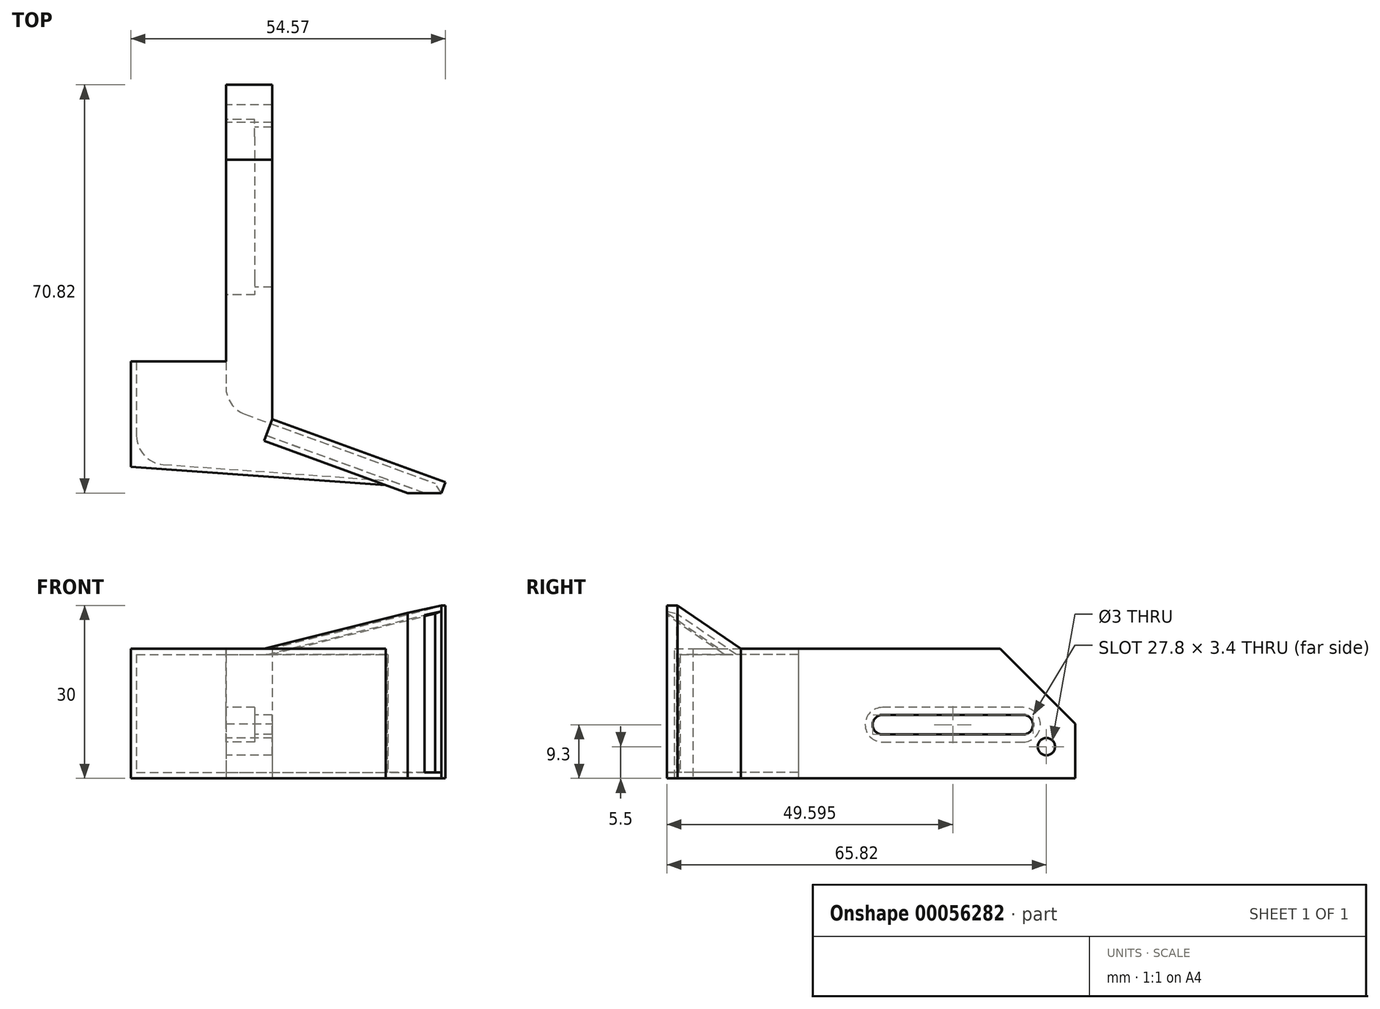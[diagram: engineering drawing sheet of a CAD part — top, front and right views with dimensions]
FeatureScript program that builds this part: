
annotation { "Feature Type Name" : "Feature", "Feature Type Description" : "" }
export const myFeature = defineFeature(function(context is Context, id is Id, definition is map)
    precondition{}
    {
        {
            var Q0;
            Q0=qCreatedBy(makeId("Top.planeOp"),FACE);
            var sketch = newSketch(context, id + "F0", { "sketchPlane" : qUnion([Q0])});
            skLineSegment(sketch, "E0", {"start": v(0, 0) * mm, "end": v(0, 18.27) * mm});
            skLineSegment(sketch, "E1", {"start": v(0, 18.27) * mm, "end": v(24.5, 18.27) * mm});
            skLineSegment(sketch, "E2", {"start": v(24.5, 18.27) * mm, "end": v(24.5, 8.27) * mm});
            skLineSegment(sketch, "E3", {"start": v(24.5, 8.27) * mm, "end": v(48.9, -0.61) * mm});
            skLineSegment(sketch, "E4", {"start": v(48.9, -0.61) * mm, "end": v(47.88, -3.43) * mm});
            skLineSegment(sketch, "E5", {"start": v(47.88, -3.43) * mm, "end": v(0, 0) * mm});
            skSolve(sketch);
        }
        {
            var Q0;
            Q0=qSketchRegion(id+"F0",true);
            extrude(context, id + "F1", {"entities" : qUnion([Q0]), "depth" : 1 * mm});
        }
        {
            var Q0;
            Q0=makeQuery(id+"F1.opExtrude","CAP_FACE",FACE,{"disambiguationData":[OSD([sQuery(id+"F0.wireOp",EDGE,"E0"),sQuery(id+"F0.wireOp",EDGE,"E1"),sQuery(id+"F0.wireOp",EDGE,"E2"),sQuery(id+"F0.wireOp",EDGE,"E3"),sQuery(id+"F0.wireOp",EDGE,"E4"),sQuery(id+"F0.wireOp",EDGE,"E5")])],"isStart":false});
            var sketch = newSketch(context, id + "F2", { "sketchPlane" : qUnion([Q0])});
            skLineSegment(sketch, "E6", {"start": v(0, 18.27) * mm, "end": v(1, 18.27) * mm});
            skLineSegment(sketch, "E7", {"start": v(1, 18.27) * mm, "end": v(1, 0.73) * mm});
            skLineSegment(sketch, "E8", {"start": v(1, 0.73) * mm, "end": v(48.16, -2.65) * mm});
            skLineSegment(sketch, "E9", {"start": v(48.16, -2.65) * mm, "end": v(47.88, -3.43) * mm});
            skLineSegment(sketch, "E10", {"start": v(24.5, 18.27) * mm, "end": v(16.5, 18.27) * mm});
            skLineSegment(sketch, "E11", {"start": v(16.5, 18.27) * mm, "end": v(16.5, 10.33) * mm});
            skLineSegment(sketch, "E12", {"start": v(16.5, 10.33) * mm, "end": v(48.63, -1.36) * mm});
            skSolve(sketch);
        }
        {
            var Q0;
            Q0=qSketchRegion(id+"F2",true);
            var Q1;
            Q1=makeQuery(id+"F2.imprint","IMPRINT",FACE,{"disambiguationData":[TD([[makeQuery(id+"F2.imprint","IMPRINT",EDGE,{"derivedFrom":sQuery(id+"F2.wireOp",EDGE,"E6")}),-1.0]])]});
            var Q2;
            Q2=makeQuery(id+"F2.imprint","IMPRINT",FACE,{"disambiguationData":[TD([[makeQuery(id+"F2.imprint","IMPRINT",EDGE,{"derivedFrom":sQuery(id+"F2.wireOp",EDGE,"E10")}),-1.0]])]});
            extrude(context, id + "F3", {"entities" : qUnion([Q0, Q1, Q2]), "operationType" : NewBodyOperationType.ADD, "depth" : 20.5 * mm});
        }
        {
            var Q0;
            Q0=makeQuery(id+"F3.opExtrude","CAP_FACE",FACE,{"disambiguationData":[OSD([sQuery(id+"F0.wireOp",EDGE,"E2"),sQuery(id+"F0.wireOp",EDGE,"E3"),sQuery(id+"F0.wireOp",EDGE,"E4"),sQuery(id+"F2.wireOp",EDGE,"E10"),sQuery(id+"F2.wireOp",EDGE,"E11"),sQuery(id+"F2.wireOp",EDGE,"E12")])],"isStart":false});
            var sketch = newSketch(context, id + "F4", { "sketchPlane" : qUnion([Q0])});
            skLineSegment(sketch, "E13", {"start": v(0, 0) * mm, "end": v(0, 18.27) * mm});
            skLineSegment(sketch, "E14", {"start": v(0, 18.27) * mm, "end": v(24.5, 18.27) * mm});
            skLineSegment(sketch, "E15", {"start": v(24.5, 18.27) * mm, "end": v(24.5, 8.27) * mm});
            skLineSegment(sketch, "E16", {"start": v(24.5, 8.27) * mm, "end": v(48.9, -0.61) * mm});
            skLineSegment(sketch, "E17", {"start": v(48.9, -0.61) * mm, "end": v(47.88, -3.43) * mm});
            skLineSegment(sketch, "E18", {"start": v(47.88, -3.43) * mm, "end": v(0, 0) * mm});
            skSolve(sketch);
        }
        {
            var Q0;
            Q0=qSketchRegion(id+"F4",true);
            extrude(context, id + "F5", {"entities" : qUnion([Q0]), "operationType" : NewBodyOperationType.ADD, "depth" : 1 * mm});
        }
        {
            var Q0;
            Q0=makeQuery(id+"F1.opExtrude","CAP_FACE",FACE,{"disambiguationData":[OSD([sQuery(id+"F0.wireOp",EDGE,"E0"),sQuery(id+"F0.wireOp",EDGE,"E1"),sQuery(id+"F0.wireOp",EDGE,"E2"),sQuery(id+"F0.wireOp",EDGE,"E3"),sQuery(id+"F0.wireOp",EDGE,"E4"),sQuery(id+"F0.wireOp",EDGE,"E5")])],"isStart":true});
            var sketch = newSketch(context, id + "F6", { "sketchPlane" : qUnion([Q0])});
            skLineSegment(sketch, "E19", {"start": v(16.5, -66.27) * mm, "end": v(16.5, -18.27) * mm});
            skLineSegment(sketch, "E20.bottom", {"start": v(16.5, -18.27) * mm, "end": v(24.5, -18.27) * mm});
            skLineSegment(sketch, "E20.top", {"start": v(16.5, -66.27) * mm, "end": v(24.5, -66.27) * mm});
            skLineSegment(sketch, "E20.right", {"start": v(24.5, -18.27) * mm, "end": v(24.5, -66.27) * mm});
            skSolve(sketch);
        }
        {
            var Q0;
            Q0=qSketchRegion(id+"F6",true);
            var Q1;
            {var subQ2=sQuery(id+"F6.wireOp",EDGE,"edd6656e-1237-41b9-a912-baa1d064ff13");Q1=makeQuery(id+"F6.imprint","IMPRINT",FACE,{"disambiguationData":[TD([[makeQuery(id+"F6.imprint","IMPRINT",EDGE,{"derivedFrom":subQ2}),-1.0]])]});}
            var Q2;
            Q2=makeQuery(id+"F5.opExtrude","CAP_FACE",FACE,{"disambiguationData":[OSD([sQuery(id+"F4.wireOp",EDGE,"E13"),sQuery(id+"F4.wireOp",EDGE,"E14"),sQuery(id+"F4.wireOp",EDGE,"E15"),sQuery(id+"F4.wireOp",EDGE,"E16"),sQuery(id+"F4.wireOp",EDGE,"E17"),sQuery(id+"F4.wireOp",EDGE,"E18")])],"isStart":false});
            extrude(context, id + "F7", {"entities" : qUnion([Q0, Q1]), "operationType" : NewBodyOperationType.ADD, "endBound" : BoundingType.UP_TO_SURFACE, "oppositeDirection" : true, "endBoundEntityFace" : qUnion([Q2]), "depth" : 22 * mm});
        }
        {
            var Q0;
            Q0=makeQuery(id+"F7.boolean.opBoolean","MERGE",FACE,{"derivedFrom":[makeQuery(id+"F3.opExtrude","SWEPT_FACE",FACE,{"disambiguationData":[OSD([sQuery(id+"F2.wireOp",EDGE,"E11")])]}),makeQuery(id+"F7.opExtrude","SWEPT_FACE",FACE,{"disambiguationData":[OSD([sQuery(id+"F6.wireOp",EDGE,"E19")])]})]});
            var sketch = newSketch(context, id + "F8", { "sketchPlane" : qUnion([Q0])});
            skCircle(sketch, "E21", {"center": v(-61.27, 5.5) * mm, "radius": 1.5 * mm});
            skPoint(sketch, "E21.centerSnap0", {"position": v(-66.27, 11.25) * mm});
            skArc(sketch, "E22", {"start": v(-57.25, 11) * mm, "mid": v(-58.95, 9.3) * mm, "end": v(-57.25, 7.6) * mm});
            skArc(sketch, "E23", {"start": v(-32.85, 7.6) * mm, "mid": v(-31.15, 9.3) * mm, "end": v(-32.85, 11) * mm});
            skLineSegment(sketch, "E24", {"start": v(-57.25, 11) * mm, "end": v(-32.85, 11) * mm});
            skLineSegment(sketch, "E25", {"start": v(-57.25, 7.6) * mm, "end": v(-32.85, 7.6) * mm});
            skArc(sketch, "E26", {"start": v(-57.25, 12.3) * mm, "mid": v(-60.25, 9.3) * mm, "end": v(-57.25, 6.3) * mm});
            skArc(sketch, "E27", {"start": v(-32.85, 6.3) * mm, "mid": v(-29.85, 9.3) * mm, "end": v(-32.85, 12.3) * mm});
            skLineSegment(sketch, "E28", {"start": v(-57.25, 12.3) * mm, "end": v(-32.85, 12.3) * mm});
            skLineSegment(sketch, "E29", {"start": v(-32.85, 6.3) * mm, "end": v(-57.25, 6.3) * mm});
            skSolve(sketch);
        }
        {
            var Q0;
            Q0=makeQuery(id+"F8.imprint","IMPRINT",FACE,{"disambiguationData":[TD([[makeQuery(id+"F8.imprint","IMPRINT",EDGE,{"derivedFrom":sQuery(id+"F8.wireOp",EDGE,"E21")}),1.0]])]});
            var Q1;
            Q1=makeQuery(id+"F8.imprint","IMPRINT",FACE,{"disambiguationData":[TD([[makeQuery(id+"F8.imprint","IMPRINT",EDGE,{"derivedFrom":sQuery(id+"F8.wireOp",EDGE,"E22")}),1.0]])]});
            extrude(context, id + "F9", {"entities" : qUnion([Q0, Q1]), "operationType" : NewBodyOperationType.REMOVE, "oppositeDirection" : true, "depth" : 25 * mm});
        }
        {
            var Q0;
            Q0=makeQuery(id+"F8.imprint","IMPRINT",FACE,{"disambiguationData":[TD([[makeQuery(id+"F8.imprint","IMPRINT",EDGE,{"derivedFrom":sQuery(id+"F8.wireOp",EDGE,"E22")}),-1.0]])]});
            extrude(context, id + "F10", {"entities" : qUnion([Q0]), "operationType" : NewBodyOperationType.REMOVE, "oppositeDirection" : true, "depth" : 5 * mm});
        }
        {
            var Q0;
            Q0=makeQuery(id+"F3.opExtrude","SWEPT_EDGE",EDGE,{"disambiguationData":[OSD([sQuery(id+"F2.wireOp",EDGE,"E7"),sQuery(id+"F2.wireOp",EDGE,"E8")])]});
            var Q1;
            Q1=makeQuery(id+"F3.opExtrude","SWEPT_EDGE",EDGE,{"disambiguationData":[OSD([sQuery(id+"F2.wireOp",EDGE,"E11"),sQuery(id+"F2.wireOp",EDGE,"E12")])]});
            fillet(context, id + "F11", {"entities" : qUnion([Q0, Q1]), "radius" : 5 * mm, "tangentPropagation" : true, "allowEdgeOverflow" : false});
        }
        {
            var Q0;
            Q0=makeQuery(id+"F7.opExtrude","CAP_EDGE",EDGE,{"disambiguationData":[OSD([sQuery(id+"F6.wireOp",EDGE,"E20.top")])],"isStart":false});
            chamfer(context, id + "F12", {"entities" : qUnion([Q0]), "width" : 13 * mm, "tangentPropagation" : true});
        }
        {
            var Q0;
            {var subQ0=sQuery(id+"F0.wireOp",EDGE,"E3");Q0=makeQuery(id+"F5.boolean.opBoolean","MERGE",FACE,{"derivedFrom":[makeQuery(id+"F3.boolean.opBoolean","MERGE",FACE,{"derivedFrom":[makeQuery(id+"F1.opExtrude","SWEPT_FACE",FACE,{"disambiguationData":[OSD([subQ0])]}),makeQuery(id+"F3.opExtrude","SWEPT_FACE",FACE,{"disambiguationData":[OSD([subQ0])]})]}),makeQuery(id+"F5.opExtrude","SWEPT_FACE",FACE,{"disambiguationData":[OSD([sQuery(id+"F4.wireOp",EDGE,"E16")])]})]});}
            var sketch = newSketch(context, id + "F13", { "sketchPlane" : qUnion([Q0])});
            skLineSegment(sketch, "E30", {"start": v(-52.2, 30) * mm, "end": v(-20.2, 22.5) * mm});
            skLineSegment(sketch, "E31", {"start": v(-20.2, 0) * mm, "end": v(-52.2, 0) * mm});
            skLineSegment(sketch, "E32", {"start": v(-52.2, 0) * mm, "end": v(-52.2, 30) * mm});
            skLineSegment(sketch, "E33", {"start": v(-20.2, 22.5) * mm, "end": v(-20.2, 0) * mm});
            skSolve(sketch);
        }
        {
            var Q0;
            Q0 = qSketchRegion(id + "F13", true);
            var Q1;
            Q1=makeQuery(id+"F13.imprint","IMPRINT",FACE,{"disambiguationData":[TD([[makeQuery(id+"F13.imprint","IMPRINT",EDGE,{"derivedFrom":sQuery(id+"F13.wireOp",EDGE,"E30")}),-1.0]])]});
            extrude(context, id + "F14", {"entities" : qUnion([Q0, Q1]), "operationType" : NewBodyOperationType.ADD, "oppositeDirection" : true, "depth" : 3 * mm});
        }
        {
            var Q0;
            {var subQ0=sQuery(id+"F0.wireOp",EDGE,"E3");Q0=makeQuery(id+"F14.boolean.opBoolean","MERGE",FACE,{"derivedFrom":[makeQuery(id+"F5.boolean.opBoolean","MERGE",FACE,{"derivedFrom":[makeQuery(id+"F3.boolean.opBoolean","MERGE",FACE,{"derivedFrom":[makeQuery(id+"F1.opExtrude","SWEPT_FACE",FACE,{"disambiguationData":[OSD([subQ0])]}),makeQuery(id+"F3.opExtrude","SWEPT_FACE",FACE,{"disambiguationData":[OSD([subQ0])]})]}),makeQuery(id+"F5.opExtrude","SWEPT_FACE",FACE,{"disambiguationData":[OSD([sQuery(id+"F4.wireOp",EDGE,"E16")])]})]}),makeQuery(id+"F14.opExtrude","CAP_FACE",FACE,{"disambiguationData":[OSD([sQuery(id+"F13.wireOp",EDGE,"E30"),sQuery(id+"F13.wireOp",EDGE,"E31"),sQuery(id+"F13.wireOp",EDGE,"E32"),sQuery(id+"F13.wireOp",EDGE,"E33")])],"isStart":true})]});}
            var sketch = newSketch(context, id + "F15", { "sketchPlane" : qUnion([Q0])});
            skLineSegment(sketch, "E34", {"start": v(-20.2, 21.47) * mm, "end": v(-20.2, 1) * mm});
            skLineSegment(sketch, "E35", {"start": v(-20.2, 1) * mm, "end": v(-52.2, 1) * mm});
            skLineSegment(sketch, "E36", {"start": v(-52.2, 1) * mm, "end": v(-52.2, 28.97) * mm});
            skLineSegment(sketch, "E37", {"start": v(-52.2, 28.97) * mm, "end": v(-20.2, 21.47) * mm});
            skSolve(sketch);
        }
        {
            var Q0;
            Q0 = qSketchRegion(id + "F15", true);
            var Q1;
            {var subQ1=sQuery(id+"F0.wireOp",EDGE,"E5");var subQ2=sQuery(id+"F13.wireOp",EDGE,"E31");var subQ7=sQuery(id+"F13.wireOp",EDGE,"E30");var subQ8=sQuery(id+"F13.wireOp",EDGE,"E32");Q1=makeQuery(id+"F14.boolean.opBoolean","SPLIT",FACE,{"disambiguationData":[TD([makeQuery(id+"F1.opExtrude","SWEPT_FACE",FACE,{"disambiguationData":[OSD([subQ1])]})])],"derivedFrom":makeQuery(id+"F14.opExtrude","CAP_FACE",FACE,{"disambiguationData":[OSD([subQ7,subQ2,subQ8,sQuery(id+"F13.wireOp",EDGE,"E33")])],"isStart":false})});}
            extrude(context, id + "F16", {"entities" : qUnion([Q0]), "operationType" : NewBodyOperationType.REMOVE, "endBound" : BoundingType.UP_TO_SURFACE, "oppositeDirection" : true, "endBoundEntityFace" : qUnion([Q1]), "depth" : 25 * mm});
        }
        {
            var Q0;
            Q0=makeQuery(id+"F16.boolean.opBoolean","COPY",FACE,{"derivedFrom":makeQuery(id+"F16.opExtrude","SWEPT_FACE",FACE,{"disambiguationData":[OSD([sQuery(id+"F15.wireOp",EDGE,"E34")])]})});
            var Q1;
            {var subQ7=sQuery(id+"F13.wireOp",EDGE,"E32");var subQ8=sQuery(id+"F13.wireOp",EDGE,"E31");Q1=makeQuery(id+"F16.boolean.opBoolean","SPLIT",FACE,{"disambiguationData":[TD([makeQuery(id+"F14.opExtrude","SWEPT_FACE",FACE,{"disambiguationData":[OSD([subQ8])]})])],"derivedFrom":makeQuery(id+"F14.opExtrude","SWEPT_FACE",FACE,{"disambiguationData":[OSD([subQ7])]})});}
            extrude(context, id + "F17", {"entities" : qUnion([Q0]), "operationType" : NewBodyOperationType.ADD, "endBound" : BoundingType.UP_TO_SURFACE, "endBoundEntityFace" : qUnion([Q1]), "depth" : 25 * mm});
        }
        {
            var Q0;
            Q0=makeQuery(id+"F17.opExtrude","SWEPT_FACE",FACE,{"disambiguationData":[OSD([sQuery(id+"F0.wireOp",EDGE,"E2"),sQuery(id+"F0.wireOp",EDGE,"E3"),sQuery(id+"F4.wireOp",EDGE,"E15"),sQuery(id+"F4.wireOp",EDGE,"E16"),sQuery(id+"F15.wireOp",EDGE,"E34"),sQuery(id+"F15.wireOp",EDGE,"E37")])]});
            var Q1;
            Q1=makeQuery(id+"F16.boolean.opBoolean","COPY",FACE,{"derivedFrom":makeQuery(id+"F16.opExtrude","SWEPT_FACE",FACE,{"disambiguationData":[OSD([sQuery(id+"F15.wireOp",EDGE,"E37")])]})});
            extrude(context, id + "F18", {"entities" : qUnion([Q0]), "operationType" : NewBodyOperationType.ADD, "endBound" : BoundingType.UP_TO_SURFACE, "endBoundEntityFace" : qUnion([Q1]), "depth" : 25 * mm});
        }
        {
            var Q0;
            {var subQ0=sQuery(id+"F13.wireOp",EDGE,"E30");var subQ1=makeQuery(id+"F14.opExtrude","SWEPT_FACE",FACE,{"disambiguationData":[OSD([subQ0])]});var subQ7=sQuery(id+"F13.wireOp",EDGE,"E32");var subQ12=sQuery(id+"F0.wireOp",EDGE,"E5");var subQ13=sQuery(id+"F13.wireOp",EDGE,"E31");Q0=makeQuery(id+"F16.boolean.opBoolean","SPLIT",FACE,{"disambiguationData":[TD([subQ1])],"derivedFrom":makeQuery(id+"F14.boolean.opBoolean","SPLIT",FACE,{"disambiguationData":[TD([makeQuery(id+"F1.opExtrude","SWEPT_FACE",FACE,{"disambiguationData":[OSD([subQ12])]})])],"derivedFrom":makeQuery(id+"F14.opExtrude","CAP_FACE",FACE,{"disambiguationData":[OSD([subQ0,subQ13,subQ7,sQuery(id+"F13.wireOp",EDGE,"E33")])],"isStart":false})})});}
            var Q1;
            {var subQ0=sQuery(id+"F0.wireOp",EDGE,"E5");var subQ2=sQuery(id+"F13.wireOp",EDGE,"E31");var subQ4=makeQuery(id+"F1.opExtrude","SWEPT_FACE",FACE,{"disambiguationData":[OSD([subQ0])]});var subQ18=sQuery(id+"F13.wireOp",EDGE,"E32");var subQ21=sQuery(id+"F13.wireOp",EDGE,"E30");Q1=makeQuery(id+"F16.boolean.opBoolean","SPLIT",FACE,{"disambiguationData":[TD([subQ4])],"derivedFrom":makeQuery(id+"F14.boolean.opBoolean","SPLIT",FACE,{"disambiguationData":[TD([subQ4])],"derivedFrom":makeQuery(id+"F14.opExtrude","CAP_FACE",FACE,{"disambiguationData":[OSD([subQ21,subQ2,subQ18,sQuery(id+"F13.wireOp",EDGE,"E33")])],"isStart":false})})});}
            extrude(context, id + "F19", {"entities" : qUnion([Q0, Q1]), "operationType" : NewBodyOperationType.ADD, "depth" : 1 * mm});
        }
        {
            var Q0;
            Q0=makeQuery(id+"F19.opExtrude","SWEPT_FACE",FACE,{"disambiguationData":[OSD([sQuery(id+"F0.wireOp",EDGE,"E4"),sQuery(id+"F0.wireOp",EDGE,"E5"),sQuery(id+"F2.wireOp",EDGE,"E9"),sQuery(id+"F4.wireOp",EDGE,"E17"),sQuery(id+"F4.wireOp",EDGE,"E18")])]});
            var Q1;
            {var subQ0=sQuery(id+"F0.wireOp",EDGE,"E5");Q1=makeQuery(id+"F5.boolean.opBoolean","MERGE",FACE,{"derivedFrom":[makeQuery(id+"F3.boolean.opBoolean","MERGE",FACE,{"derivedFrom":[makeQuery(id+"F1.opExtrude","SWEPT_FACE",FACE,{"disambiguationData":[OSD([subQ0])]}),makeQuery(id+"F3.opExtrude","SWEPT_FACE",FACE,{"disambiguationData":[OSD([subQ0])]})]}),makeQuery(id+"F5.opExtrude","SWEPT_FACE",FACE,{"disambiguationData":[OSD([sQuery(id+"F4.wireOp",EDGE,"E18")])]})]});}
            extrude(context, id + "F20", {"entities" : qUnion([Q0]), "operationType" : NewBodyOperationType.ADD, "endBound" : BoundingType.UP_TO_SURFACE, "endBoundEntityFace" : qUnion([Q1]), "depth" : 25 * mm});
        }
        {
            var Q0;
            {var subQ0=sQuery(id+"F4.wireOp",EDGE,"E18");var subQ1=sQuery(id+"F4.wireOp",EDGE,"E17");var subQ2=sQuery(id+"F0.wireOp",EDGE,"E5");var subQ3=sQuery(id+"F0.wireOp",EDGE,"E4");var subQ5=sQuery(id+"F13.wireOp",EDGE,"E31");var subQ7=makeQuery(id+"F1.opExtrude","SWEPT_FACE",FACE,{"disambiguationData":[OSD([subQ2])]});var subQ19=sQuery(id+"F13.wireOp",EDGE,"E32");var subQ22=sQuery(id+"F13.wireOp",EDGE,"E30");var subQ23=sQuery(id+"F13.wireOp",EDGE,"E33");Q0=makeQuery(id+"F20.boolean.opBoolean","MERGE",FACE,{"derivedFrom":[makeQuery(id+"F19.opExtrude","CAP_FACE",FACE,{"disambiguationData":[OSD([subQ22,subQ5,subQ19,subQ23]),TDD([makeQuery(id+"F16.boolean.opBoolean","SPLIT",FACE,{"disambiguationData":[TD([subQ7])],"derivedFrom":makeQuery(id+"F14.boolean.opBoolean","SPLIT",FACE,{"disambiguationData":[TD([subQ7])],"derivedFrom":makeQuery(id+"F14.opExtrude","CAP_FACE",FACE,{"disambiguationData":[OSD([subQ22,subQ5,subQ19,subQ23])],"isStart":false})})})])],"isStart":false}),makeQuery(id+"F20.opExtrude","SWEPT_FACE",FACE,{"disambiguationData":[OSD([subQ3,subQ2,sQuery(id+"F2.wireOp",EDGE,"E9"),subQ1,subQ0])]})]});}
            var sketch = newSketch(context, id + "F21", { "sketchPlane" : qUnion([Q0])});
            skLineSegment(sketch, "E38.bottom", {"start": v(52.2, 0) * mm, "end": v(42.65, 0) * mm});
            skLineSegment(sketch, "E38.left", {"start": v(52.2, 0) * mm, "end": v(52.2, 30) * mm});
            skLineSegment(sketch, "E39", {"start": v(20.2, 22.5) * mm, "end": v(52.2, 30) * mm});
            skLineSegment(sketch, "E40", {"start": v(20.2, 22.5) * mm, "end": v(42.65, 22.5) * mm});
            skLineSegment(sketch, "E41", {"start": v(42.65, 22.5) * mm, "end": v(42.65, 0) * mm});
            skSolve(sketch);
        }
        {
            var Q0;
            {var subQ4=sQuery(id+"F21.wireOp",EDGE,"E39");Q0=makeQuery(id+"F21.imprint","IMPRINT",FACE,{"disambiguationData":[TD([[makeQuery(id+"F21.imprint","IMPRINT",EDGE,{"derivedFrom":subQ4}),-1.0]])]});}
            extrude(context, id + "F22", {"entities" : qUnion([Q0]), "operationType" : NewBodyOperationType.ADD, "oppositeDirection" : true, "depth" : 1 * mm});
        }
        {
            var Q0;
            {var subQ0=sQuery(id+"F0.wireOp",EDGE,"E5");var subQ1=sQuery(id+"F0.wireOp",EDGE,"E4");var subQ2=sQuery(id+"F13.wireOp",EDGE,"E31");Q0=makeQuery(id+"F20.boolean.opBoolean","MERGE",FACE,{"derivedFrom":[makeQuery(id+"F19.boolean.opBoolean","MERGE",FACE,{"derivedFrom":[makeQuery(id+"F14.boolean.opBoolean","MERGE",FACE,{"derivedFrom":[makeQuery(id+"F7.boolean.opBoolean","MERGE",FACE,{"derivedFrom":[makeQuery(id+"F1.opExtrude","CAP_FACE",FACE,{"disambiguationData":[OSD([sQuery(id+"F0.wireOp",EDGE,"E0"),sQuery(id+"F0.wireOp",EDGE,"E1"),sQuery(id+"F0.wireOp",EDGE,"E2"),sQuery(id+"F0.wireOp",EDGE,"E3"),subQ1,subQ0])],"isStart":true}),makeQuery(id+"F7.opExtrude","CAP_FACE",FACE,{"disambiguationData":[OSD([sQuery(id+"F6.wireOp",EDGE,"E19"),sQuery(id+"F6.wireOp",EDGE,"E20.bottom"),sQuery(id+"F6.wireOp",EDGE,"E20.top"),sQuery(id+"F6.wireOp",EDGE,"E20.right")])],"isStart":true})]}),makeQuery(id+"F14.opExtrude","SWEPT_FACE",FACE,{"disambiguationData":[OSD([subQ2])]})]}),makeQuery(id+"F19.opExtrude","SWEPT_FACE",FACE,{"disambiguationData":[OSD([subQ2])]})]}),makeQuery(id+"F20.opExtrude","SWEPT_FACE",FACE,{"disambiguationData":[OSD([subQ1,subQ0])]})]});}
            var sketch = newSketch(context, id + "F23", { "sketchPlane" : qUnion([Q0])});
            skLineSegment(sketch, "E42", {"start": v(53.89, 4.55) * mm, "end": v(48.04, 4.55) * mm});
            skLineSegment(sketch, "E43", {"start": v(48.04, 4.55) * mm, "end": v(53.2, 6.43) * mm});
            skLineSegment(sketch, "E44", {"start": v(53.89, 4.55) * mm, "end": v(53.2, 6.43) * mm});
            skSolve(sketch);
        }
        {
            var Q0;
            Q0=makeQuery(id+"F23.imprint","IMPRINT",FACE,{"disambiguationData":[TD([[makeQuery(id+"F23.imprint","IMPRINT",EDGE,{"derivedFrom":sQuery(id+"F23.wireOp",EDGE,"E42")}),-1.0]])]});
            var Q1;
            {var subQ0=sQuery(id+"F13.wireOp",EDGE,"E30");Q1=makeQuery(id+"F19.boolean.opBoolean","MERGE",FACE,{"derivedFrom":[makeQuery(id+"F14.opExtrude","SWEPT_FACE",FACE,{"disambiguationData":[OSD([subQ0])]}),makeQuery(id+"F19.opExtrude","SWEPT_FACE",FACE,{"disambiguationData":[OSD([subQ0])]})]});}
            extrude(context, id + "F24", {"entities" : qUnion([Q0]), "operationType" : NewBodyOperationType.REMOVE, "endBound" : BoundingType.UP_TO_SURFACE, "oppositeDirection" : true, "endBoundEntityFace" : qUnion([Q1]), "depth" : 25 * mm});
        }
        {
            var Q0;
            {var subQ0=sQuery(id+"F15.wireOp",EDGE,"E35");var subQ1=sQuery(id+"F0.wireOp",EDGE,"E5");var subQ2=sQuery(id+"F0.wireOp",EDGE,"E4");var subQ3=sQuery(id+"F0.wireOp",EDGE,"E3");var subQ4=sQuery(id+"F0.wireOp",EDGE,"E2");var subQ5=sQuery(id+"F0.wireOp",EDGE,"E1");var subQ6=sQuery(id+"F0.wireOp",EDGE,"E0");Q0=makeQuery(id+"F20.boolean.opBoolean","MERGE",FACE,{"derivedFrom":[makeQuery(id+"F19.boolean.opBoolean","MERGE",FACE,{"derivedFrom":[makeQuery(id+"F16.boolean.opBoolean","MERGE",FACE,{"derivedFrom":[makeQuery(id+"F1.opExtrude","CAP_FACE",FACE,{"disambiguationData":[OSD([subQ6,subQ5,subQ4,subQ3,subQ2,subQ1])],"isStart":false}),makeQuery(id+"F16.opExtrude","SWEPT_FACE",FACE,{"disambiguationData":[OSD([subQ0])]})]}),makeQuery(id+"F19.opExtrude","SWEPT_FACE",FACE,{"disambiguationData":[OSD([subQ0])]})]}),makeQuery(id+"F20.opExtrude","SWEPT_FACE",FACE,{"disambiguationData":[OSD([subQ6,subQ5,subQ4,subQ3,subQ2,subQ1,sQuery(id+"F4.wireOp",EDGE,"E18"),sQuery(id+"F13.wireOp",EDGE,"E30"),sQuery(id+"F13.wireOp",EDGE,"E31"),sQuery(id+"F13.wireOp",EDGE,"E32"),sQuery(id+"F13.wireOp",EDGE,"E33"),sQuery(id+"F15.wireOp",EDGE,"E34"),subQ0,sQuery(id+"F15.wireOp",EDGE,"E36"),sQuery(id+"F15.wireOp",EDGE,"E37")])]})]});}
            var sketch = newSketch(context, id + "F25", { "sketchPlane" : qUnion([Q0])});
            skLineSegment(sketch, "E45", {"start": v(53.89, -4.55) * mm, "end": v(54.3, -3.43) * mm});
            skLineSegment(sketch, "E46", {"start": v(54.3, -3.43) * mm, "end": v(52.78, -2.88) * mm});
            skLineSegment(sketch, "E47", {"start": v(52.78, -2.88) * mm, "end": v(53.89, -4.55) * mm});
            skSolve(sketch);
        }
        {
            var Q0;
            Q0 = qSketchRegion(id + "F25", true);
            var Q1;
            {var subQ0=sQuery(id+"F15.wireOp",EDGE,"E37");Q1=makeQuery(id+"F19.boolean.opBoolean","MERGE",FACE,{"derivedFrom":[makeQuery(id+"F16.boolean.opBoolean","COPY",FACE,{"derivedFrom":makeQuery(id+"F16.opExtrude","SWEPT_FACE",FACE,{"disambiguationData":[OSD([subQ0])]})}),makeQuery(id+"F19.opExtrude","SWEPT_FACE",FACE,{"disambiguationData":[OSD([subQ0])]})]});}
            extrude(context, id + "F26", {"entities" : qUnion([Q0]), "operationType" : NewBodyOperationType.ADD, "endBound" : BoundingType.UP_TO_SURFACE, "endBoundEntityFace" : qUnion([Q1]), "depth" : 25 * mm});
        }
    });
